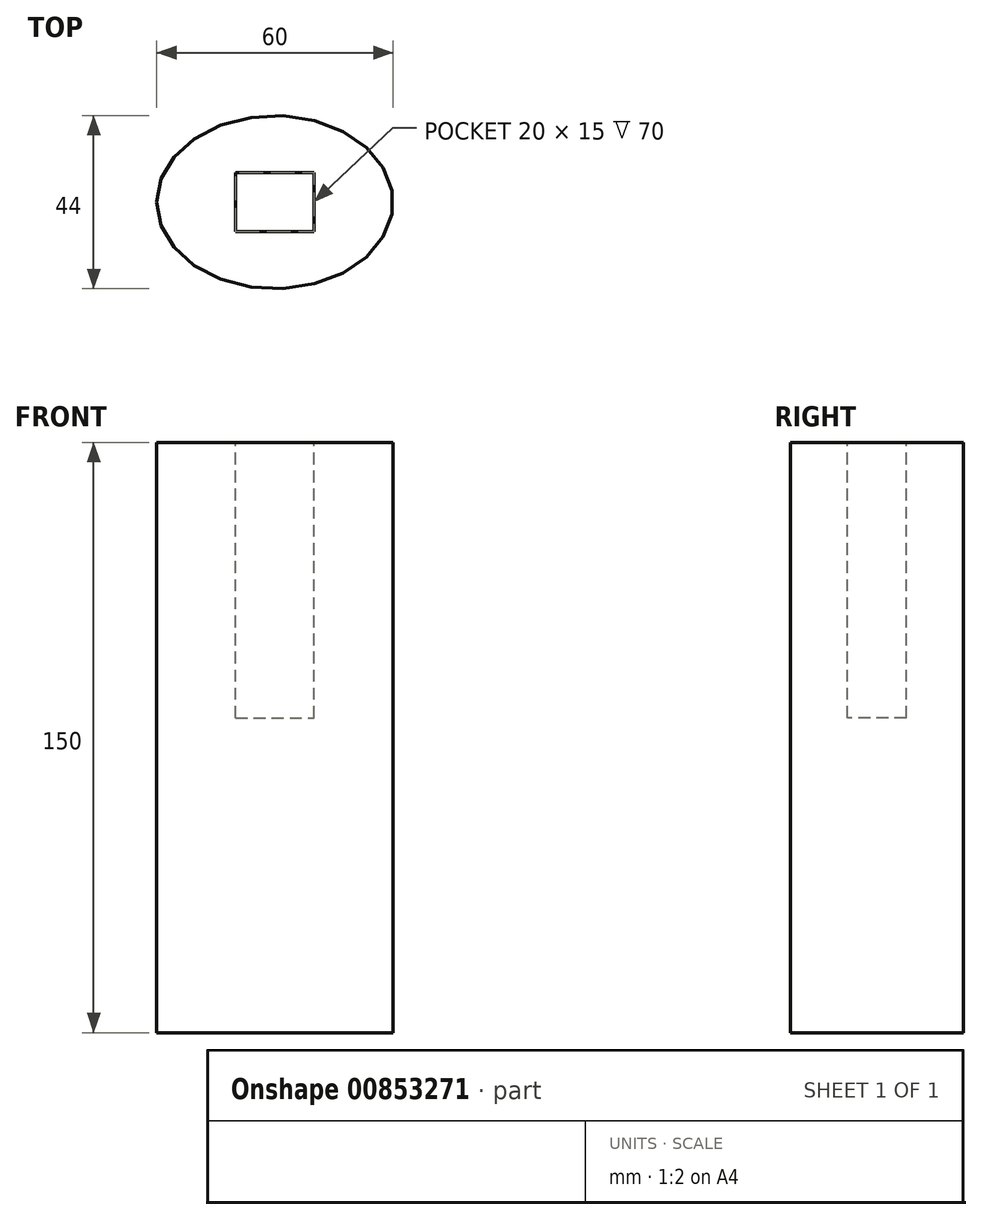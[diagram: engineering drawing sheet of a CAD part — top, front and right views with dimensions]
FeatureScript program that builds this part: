
annotation { "Feature Type Name" : "Feature", "Feature Type Description" : "" }
export const myFeature = defineFeature(function(context is Context, id is Id, definition is map)
    precondition{}
    {
        {
            var Q0;
            Q0=qCreatedBy(makeId("Top.planeOp"),FACE);
            var sketch = newSketch(context, id + "F0", { "sketchPlane" : qUnion([Q0])});
            skEllipse(sketch, "E0", {"center": v(0, 0) * mm, "majorRadius": 30 * mm, "minorRadius": 22 * mm, "majorAxis": v(-1, 0)});
            skSolve(sketch);
        }
        {
            var Q0;
            Q0 = qSketchRegion(id + "F0", true);
            extrude(context, id + "F1", {"entities" : qUnion([Q0]), "depth" : 150 * mm, "offsetDistance" : 25 * mm});
        }
        {
            var Q0;
            Q0=makeQuery(id+"F1.opExtrude","CAP_FACE",FACE,{"disambiguationData":[OSD([sQuery(id+"F0.wireOp",EDGE,"E0")])],"isStart":true});
            var sketch = newSketch(context, id + "F2", { "sketchPlane" : qUnion([Q0])});
            skLineSegment(sketch, "E1", {"start": v(0, 0) * mm, "end": v(-30, 0) * mm});
            skSolve(sketch);
        }
        {
            var Q0;
            Q0=makeQuery(id+"F1.opExtrude","CAP_FACE",FACE,{"disambiguationData":[OSD([sQuery(id+"F0.wireOp",EDGE,"E0")])],"isStart":false});
            var sketch = newSketch(context, id + "F3", { "sketchPlane" : qUnion([Q0])});
            skLineSegment(sketch, "E2.bottom", {"start": v(-10, 7.5) * mm, "end": v(10, 7.5) * mm});
            skLineSegment(sketch, "E2.top", {"start": v(-10, -7.5) * mm, "end": v(10, -7.5) * mm});
            skLineSegment(sketch, "E2.left", {"start": v(-10, 7.5) * mm, "end": v(-10, -7.5) * mm});
            skLineSegment(sketch, "E2.right", {"start": v(10, 7.5) * mm, "end": v(10, -7.5) * mm});
            skSolve(sketch);
        }
        {
            var Q0;
            Q0=makeQuery(id+"F3.imprint","IMPRINT",FACE,{"disambiguationData":[TD([[makeQuery(id+"F3.imprint","IMPRINT",EDGE,{"derivedFrom":sQuery(id+"F3.wireOp",EDGE,"5UnWocxb-x9tC-lAWQ-Y686-vbfYepnI5Yeo.bottom")}),-1.0]])]});
            var Q1;
            Q1=makeQuery(id+"F3.imprint","IMPRINT",FACE,{"disambiguationData":[TD([[makeQuery(id+"F3.imprint","IMPRINT",EDGE,{"derivedFrom":sQuery(id+"F3.wireOp",EDGE,"E2.bottom")}),-1.0]])]});
            extrude(context, id + "F4", {"entities" : qUnion([Q0, Q1]), "operationType" : NewBodyOperationType.REMOVE, "oppositeDirection" : true, "depth" : 70 * mm, "offsetDistance" : 25 * mm});
        }
    });
